# Revit family: ВКП_Eng
name_source: partatom
category: Mechanical Equipment
units: mm (PartAtom-declared; Revit-internal decimal feet)

## family parameters
Always vertical = Yes
Classification = None
Cut with Voids When Loaded = No
Part Type = Normal
Room Calculation Point = No
Round Connector Dimension = Use Diameter
Shared = No
Work Plane-Based = No

## types (11) — shared parameters
00_20_Manufacturer = Vents
00_20_Name = Inline centrifugal fan
Casing Material = Steel, galvanized
Description = For rectangular ducts
Load Classification = HVAC
Maintenance zone material = <By Category>
Manufacturer = Vents
URL = https://ventilation-system.com

## per-type parameters (varying)
- VKP 2E 400x200: Alfa=90.00°; Amperage=1 A; B=400 mm; Be=40 mm  [stored 0.131234 ft]; Default Elevation=0 mm  [stored 0 ft]; Electrical box=No; Frame=Frame : 400x200; H=200 mm  [stored 0.656168 ft]; He=200 mm  [stored 0.656168 ft]; Height=230 mm  [stored 0.754593 ft]; L=500 mm; Le=25 mm  [stored 0.082021 ft]; Length=500 mm; Maximum Air Flow=258.0 L/s; Number of Fase=1; Power=138 W; Voltage=230 V; Weight=11.25 kg; Width=400 mm; b=67 mm; b1=160 mm  [stored 0.524934 ft]; b2=396 mm; b3=100 mm  [stored 0.328084 ft]; h=67 mm; h1=95 mm  [stored 0.31168 ft]; h2=198 mm  [stored 0.649606 ft]; h3=100 mm  [stored 0.328084 ft]; l=107 mm; l1=210 mm  [stored 0.688976 ft]; l3=150 mm  [stored 0.492126 ft]; r1=100 mm  [stored 0.328084 ft]; r2=80 mm  [stored 0.262467 ft]; r3=13 mm; Сonnector=Yes
- VKP 4D 800x500: Alfa=0.00°; Amperage=3 A; B=800 mm; Be=700 mm; Default Elevation=0 mm  [stored 0 ft]; Electrical box=Yes; Frame=Frame : 800x500; H=500 mm; He=525 mm; Height=550 mm; L=903 mm; Le=50 mm  [stored 0.164042 ft]; Length=903 mm; Maximum Air Flow=2170.0 L/s; Number of Fase=3; Power=1508 W; Voltage=400 V; Weight=54.00 kg; Width=800 mm; b=133 mm; b1=360 mm; b2=796 mm; b3=300 mm; h=167 mm; h1=238 mm; h2=498 mm; h3=250 mm; l=194 mm; l1=412 mm; l3=352 mm; r1=250 mm; r2=200 mm  [stored 0.656168 ft]; r3=33 mm; Сonnector=No
- VKP 2E 500x250: Alfa=90.00°; Amperage=1 A; B=500 mm; Be=40 mm  [stored 0.131234 ft]; Default Elevation=0 mm  [stored 0 ft]; Electrical box=No; Frame=Frame : 500x250; H=250 mm; He=250 mm; Height=280 mm; L=640 mm; Le=25 mm  [stored 0.082021 ft]; Length=640 mm; Maximum Air Flow=478.0 L/s; Number of Fase=1; Power=305 W; Voltage=230 V; Weight=17.88 kg; Width=500 mm; b=83 mm; b1=210 mm  [stored 0.688976 ft]; b2=496 mm; b3=150 mm  [stored 0.492126 ft]; h=83 mm; h1=119 mm; h2=248 mm; h3=125 mm  [stored 0.410105 ft]; l=137 mm; l1=280 mm; l3=220 mm  [stored 0.721785 ft]; r1=125 mm  [stored 0.410105 ft]; r2=100 mm  [stored 0.328084 ft]; r3=17 mm; Сonnector=Yes
- VKP 4E 500x300: Alfa=90.00°; Amperage=1 A; B=500 mm; Be=40 mm  [stored 0.131234 ft]; Default Elevation=0 mm  [stored 0 ft]; Electrical box=No; Frame=Frame : 500x300; H=300 mm; He=300 mm; Height=330 mm; L=680 mm; Le=25 mm  [stored 0.082021 ft]; Length=680 mm; Maximum Air Flow=470.0 L/s; Number of Fase=1; Power=140 W; Voltage=230 V; Weight=19.80 kg; Width=500 mm; b=83 mm; b1=210 mm  [stored 0.688976 ft]; b2=496 mm; b3=150 mm  [stored 0.492126 ft]; h=100 mm  [stored 0.328084 ft]; h1=143 mm; h2=298 mm; h3=150 mm  [stored 0.492126 ft]; l=146 mm; l1=300 mm; l3=240 mm; r1=150 mm  [stored 0.492126 ft]; r2=120 mm  [stored 0.393701 ft]; r3=20 mm  [stored 0.0656168 ft]; Сonnector=Yes
- VKP 4D 500x300: Alfa=90.00°; Amperage=0 A; B=500 mm; Be=40 mm  [stored 0.131234 ft]; Default Elevation=0 mm  [stored 0 ft]; Electrical box=No; Frame=Frame : 500x300; H=300 mm; He=300 mm; Height=330 mm; L=680 mm; Le=25 mm  [stored 0.082021 ft]; Length=680 mm; Maximum Air Flow=383.0 L/s; Number of Fase=3; Power=136 W; Voltage=400 V; Weight=19.80 kg; Width=500 mm; b=83 mm; b1=210 mm  [stored 0.688976 ft]; b2=496 mm; b3=150 mm  [stored 0.492126 ft]; h=100 mm  [stored 0.328084 ft]; h1=143 mm; h2=298 mm; h3=150 mm  [stored 0.492126 ft]; l=146 mm; l1=300 mm; l3=240 mm; r1=150 mm  [stored 0.492126 ft]; r2=120 mm  [stored 0.393701 ft]; r3=20 mm  [stored 0.0656168 ft]; Сonnector=Yes
- VKP 4E 600x300: Alfa=0.00°; Amperage=1 A; B=600 mm; Be=500 mm; Default Elevation=0 mm  [stored 0 ft]; Electrical box=Yes; Frame=Frame : 600x300; H=300 mm; He=325 mm; Height=350 mm; L=680 mm; Le=50 mm  [stored 0.164042 ft]; Length=680 mm; Maximum Air Flow=690.0 L/s; Number of Fase=1; Power=220 W; Voltage=230 V; Weight=27.77 kg; Width=600 mm; b=100 mm  [stored 0.328084 ft]; b1=260 mm; b2=596 mm; b3=200 mm  [stored 0.656168 ft]; h=100 mm  [stored 0.328084 ft]; h1=143 mm; h2=298 mm; h3=150 mm  [stored 0.492126 ft]; l=146 mm; l1=300 mm; l3=240 mm; r1=150 mm  [stored 0.492126 ft]; r2=120 mm  [stored 0.393701 ft]; r3=20 mm  [stored 0.0656168 ft]; Сonnector=No
- VKP 4D 600x300: Alfa=0.00°; Amperage=1 A; B=600 mm; Be=500 mm; Default Elevation=0 mm  [stored 0 ft]; Electrical box=Yes; Frame=Frame : 600x300; H=300 mm; He=325 mm; Height=350 mm; L=680 mm; Le=50 mm  [stored 0.164042 ft]; Length=680 mm; Maximum Air Flow=700.0 L/s; Number of Fase=3; Power=230 W; Voltage=400 V; Weight=27.77 kg; Width=600 mm; b=100 mm  [stored 0.328084 ft]; b1=260 mm; b2=596 mm; b3=200 mm  [stored 0.656168 ft]; h=100 mm  [stored 0.328084 ft]; h1=143 mm; h2=298 mm; h3=150 mm  [stored 0.492126 ft]; l=146 mm; l1=300 mm; l3=240 mm; r1=150 mm  [stored 0.492126 ft]; r2=120 mm  [stored 0.393701 ft]; r3=20 mm  [stored 0.0656168 ft]; Сonnector=No
- VKP 4E 600x350: Alfa=0.00°; Amperage=2 A; B=600 mm; Be=500 mm; Default Elevation=0 mm  [stored 0 ft]; Electrical box=Yes; Frame=Frame : 600x350; H=350 mm; He=375 mm; Height=400 mm; L=735 mm; Le=50 mm  [stored 0.164042 ft]; Length=735 mm; Maximum Air Flow=820.0 L/s; Number of Fase=1; Power=470 W; Voltage=230 V; Weight=36.38 kg; Width=600 mm; b=100 mm  [stored 0.328084 ft]; b1=260 mm; b2=596 mm; b3=200 mm  [stored 0.656168 ft]; h=117 mm; h1=167 mm; h2=348 mm; h3=175 mm  [stored 0.574147 ft]; l=158 mm  [stored 0.518373 ft]; l1=328 mm; l3=268 mm; r1=175 mm  [stored 0.574147 ft]; r2=140 mm  [stored 0.459318 ft]; r3=23 mm  [stored 0.0754593 ft]; Сonnector=No
- VKP 4D 600x350: Alfa=0.00°; Amperage=1 A; B=600 mm; Be=500 mm; Default Elevation=0 mm  [stored 0 ft]; Electrical box=Yes; Frame=Frame : 600x350; H=350 mm; He=375 mm; Height=400 mm; L=735 mm; Le=50 mm  [stored 0.164042 ft]; Length=735 mm; Maximum Air Flow=740.0 L/s; Number of Fase=3; Power=380 W; Voltage=400 V; Weight=36.38 kg; Width=600 mm; b=100 mm  [stored 0.328084 ft]; b1=260 mm; b2=596 mm; b3=200 mm  [stored 0.656168 ft]; h=117 mm; h1=167 mm; h2=348 mm; h3=175 mm  [stored 0.574147 ft]; l=158 mm  [stored 0.518373 ft]; l1=328 mm; l3=268 mm; r1=175 mm  [stored 0.574147 ft]; r2=140 mm  [stored 0.459318 ft]; r3=23 mm  [stored 0.0754593 ft]; Сonnector=No
- VKPS 4E 600x350: Alfa=0.00°; Amperage=2 A; B=600 mm; Be=500 mm; Default Elevation=652 mm; Electrical box=Yes; Frame=Frame : VKPS 4E 600x350; H=350 mm; He=375 mm; Height=400 mm; L=652 mm; Le=50 mm  [stored 0.164042 ft]; Length=652 mm; Maximum Air Flow=1130.0 L/s; Number of Fase=1; Power=447 W; Voltage=230 V; Weight=30.00 kg; Width=600 mm; b=100 mm  [stored 0.328084 ft]; b1=260 mm; b2=596 mm; b3=200 mm  [stored 0.656168 ft]; h=117 mm; h1=167 mm; h2=348 mm; h3=175 mm  [stored 0.574147 ft]; l=140 mm  [stored 0.459318 ft]; l1=286 mm; l3=226 mm  [stored 0.74147 ft]; r1=175 mm  [stored 0.574147 ft]; r2=140 mm  [stored 0.459318 ft]; r3=23 mm  [stored 0.0754593 ft]; Сonnector=No
- VKP 4D 700x400: Alfa=0.00°; Amperage=2 A; B=700 mm; Be=600 mm; Default Elevation=0 mm  [stored 0 ft]; Electrical box=Yes; Frame=Frame : 700x400; H=400 mm; He=425 mm; Height=450 mm; L=753 mm; Le=50 mm  [stored 0.164042 ft]; Length=753 mm; Maximum Air Flow=1550.0 L/s; Number of Fase=3; Power=828 W; Voltage=400 V; Weight=41.00 kg; Width=700 mm; b=117 mm; b1=310 mm; b2=696 mm; b3=250 mm; h=133 mm; h1=190 mm; h2=398 mm; h3=200 mm  [stored 0.656168 ft]; l=161 mm; l1=337 mm; l3=277 mm; r1=200 mm  [stored 0.656168 ft]; r2=160 mm  [stored 0.524934 ft]; r3=27 mm; Сonnector=No

note: column(s) folded — value = type name in every type: 00_20_Type

note: [stored X ft] marks values corroborated as IEEE doubles in the binary element streams (Revit-internal decimal feet)
